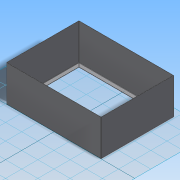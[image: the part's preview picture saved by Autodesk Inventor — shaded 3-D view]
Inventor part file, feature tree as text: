
AUTODESK INVENTOR PART (.ipt)
format: ipt  version: 2014 SP2 (Build 180246200, 246)  size: 191,488 bytes
history: native  units: in
note: dims shown in document units (in); Inventor stores cm internally (conversion verified against a paired STEP export)
features: sheet_metal_op x14, sketch x5, other x5
ambient origin geometry x8: Origin, YZ Plane, XZ Plane, XY Plane, X Axis, Y Axis, Z Axis, Center Point
bodies: Solid1 (feature_tree)
feature tree (24):
  sheet_metal_op  "Face1"
  sheet_metal_op  "Flange1"
  sheet_metal_op  "Flange2"
  sheet_metal_op  "Flange3"
  sheet_metal_op  "Flange4"
  sheet_metal_op  "Unfold1"
  sketch  "Sketch1"  dims[d0=5.875in]
  other  "Plate1"
  sketch  "Sketch2"  dims[d1=2.25in]
  other  "Plate2"
  sheet_metal_op  "Bend1"
  sheet_metal_op  "Corner1"
  sketch  "Sketch3"  dims[d2=0.02in]
  other  "Plate3"
  sheet_metal_op  "Bend2"
  sheet_metal_op  "Corner2"
  sketch  "Sketch4"  dims[d3=0.02in]
  other  "Plate4"
  sheet_metal_op  "Bend3"
  sheet_metal_op  "Corner3"
  sketch  "Sketch5"  dims[d4=0.01in d5=0.04in d6=0.02in d7=4.5in d8=90.0deg d9=0.02in d10=0.08in d11=0.02in d12=0.02in d13=0.02in d14=0.01in d15=0.04in d16=0.02in d17=5.795in d18=90.0deg d19=0.02in d20=0.08in d21=0.02in d22=0.02in d23=0.02in d24=0.01in d25=0.04in d26=0.02in d27=0.25in d28=90.0deg d29=0.02in d30=0.08in d31=0.02in d32=0.02in d33=0.02in d34=0.01in d35=0.04in d36=0.02in d37=0.25in d38=90.0deg d39=0.02in d40=0.08in d41=0.02in d42=0.02in]
  other  "Plate5"
  sheet_metal_op  "Bend4"
  sheet_metal_op  "Corner4"
